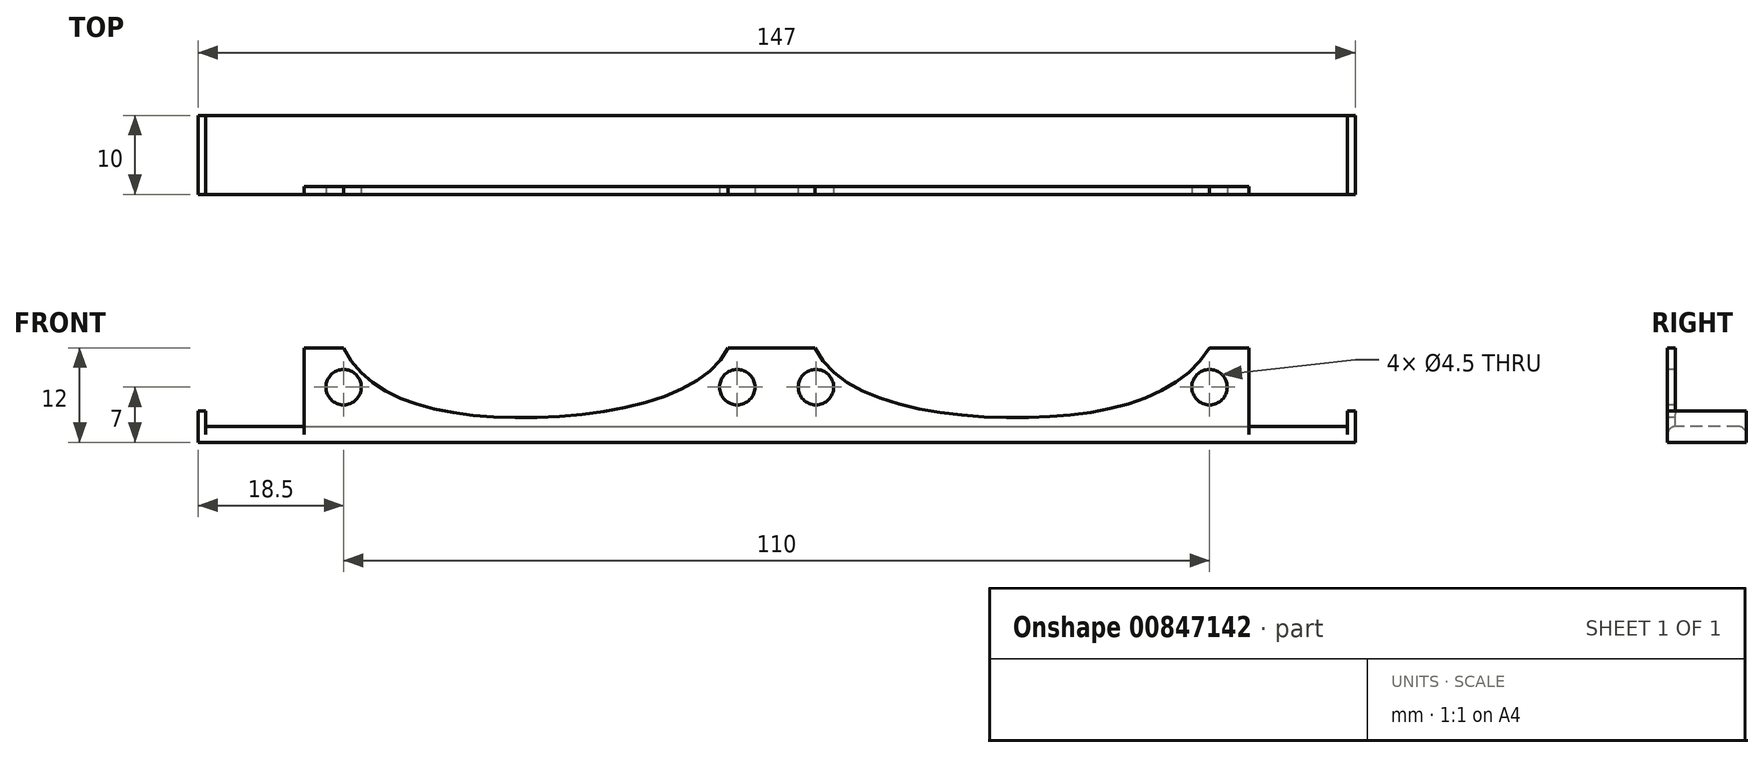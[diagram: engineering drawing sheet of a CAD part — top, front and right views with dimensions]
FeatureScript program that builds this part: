
annotation { "Feature Type Name" : "Feature", "Feature Type Description" : "" }
export const myFeature = defineFeature(function(context is Context, id is Id, definition is map)
    precondition{}
    {
        {
            var Q0;
            Q0=qCreatedBy(makeId("Front.planeOp"),FACE);
            var sketch = newSketch(context, id + "F0", { "sketchPlane" : qUnion([Q0])});
            skLineSegment(sketch, "E0.bottom", {"start": v(-60, 0) * mm, "end": v(60, 0) * mm});
            skLineSegment(sketch, "E0.top", {"start": v(-60, 10) * mm, "end": v(60, 10) * mm});
            skLineSegment(sketch, "E0.left", {"start": v(-60, 0) * mm, "end": v(-60, 10) * mm});
            skLineSegment(sketch, "E0.right", {"start": v(60, 0) * mm, "end": v(60, 10) * mm});
            skPoint(sketch, "E1", {"position": v(0, 0) * mm});
            skPoint(sketch, "E2", {"position": v(-55, 10) * mm});
            skPoint(sketch, "E3", {"position": v(55, 10) * mm});
            skPoint(sketch, "E4", {"position": v(-55, 5) * mm});
            skPoint(sketch, "E5", {"position": v(55, 5) * mm});
            skPoint(sketch, "E6", {"position": v(-5, 5) * mm});
            skPoint(sketch, "E7", {"position": v(5, 5) * mm});
            skFitSpline(sketch, "E8", {"points": [v(-55, 10) * mm, v(-33.54, 1.13) * mm, v(-6.14, 10) * mm], "startDerivative": vector(19.35, -40.47) * mm, "endDerivative": vector(17.4, 37.66) * mm});
            skFitSpline(sketch, "E9", {"points": [v(4.87, 10) * mm, v(31.43, 1.13) * mm, v(55, 10) * mm], "startDerivative": vector(19.32, -40.42) * mm, "endDerivative": vector(24.98, 40.39) * mm});
            skLineSegment(sketch, "E10.top", {"start": v(-60, -2) * mm, "end": v(60, -2) * mm});
            skLineSegment(sketch, "E10.left", {"start": v(-60, 0) * mm, "end": v(-60, -2) * mm});
            skLineSegment(sketch, "E10.right", {"start": v(60, 0) * mm, "end": v(60, -2) * mm});
            skSolve(sketch);
        }
        {
            var Q0;
            {var subQ4=sQuery(id+"F0.wireOp",EDGE,"E0.left");Q0=makeQuery(id+"F0.imprint","IMPRINT",FACE,{"disambiguationData":[TD([[makeQuery(id+"F0.imprint","IMPRINT",EDGE,{"derivedFrom":subQ4}),-1.0]])]});}
            extrude(context, id + "F1", {"entities" : qUnion([Q0]), "oppositeDirection" : true, "depth" : 1 * mm, "offsetDistance" : 25 * mm});
        }
        {
            var Q0;
            Q0=makeQuery(id+"F0.imprint","IMPRINT",FACE,{"disambiguationData":[TD([[makeQuery(id+"F0.imprint","IMPRINT",EDGE,{"derivedFrom":sQuery(id+"F0.wireOp",EDGE,"E0.bottom")}),-1.0]])]});
            extrude(context, id + "F2", {"entities" : qUnion([Q0]), "operationType" : NewBodyOperationType.ADD, "oppositeDirection" : true, "depth" : 10 * mm, "offsetDistance" : 25 * mm});
        }
        {
            var Q0;
            Q0=sQuery(id+"F0.wireOp",VERTEX,"E4");
            var Q1;
            Q1=sQuery(id+"F0.wireOp",VERTEX,"E6");
            var Q2;
            Q2=sQuery(id+"F0.wireOp",VERTEX,"E7");
            var Q3;
            Q3=sQuery(id+"F0.wireOp",VERTEX,"E5");
            var Q4;
            Q4=makeQuery(id+"F1.opExtrude","SWEPT_BODY",BODY,{"disambiguationData":[OSD([sQuery(id+"F0.wireOp",EDGE,"E0.top"),sQuery(id+"F0.wireOp",EDGE,"E0.left"),sQuery(id+"F0.wireOp",EDGE,"E0.right"),sQuery(id+"F0.wireOp",EDGE,"E8"),sQuery(id+"F0.wireOp",EDGE,"E9"),sQuery(id+"F0.wireOp",EDGE,"E0.bottom")])]});
            hole(context, id + "F3", {"style" : HoleStyle.SIMPLE, "endStyle" : HoleEndStyle.BLIND, "holeDiameter" : 4.5 * mm, "majorDiameter" : 5 * mm, "holeDepth" : 2 * mm, "isTappedThrough" : true, "tappedDepth" : 12 * mm, "tapClearance" : 3, "locations" : qUnion([Q0, Q1, Q2, Q3]), "scope" : qUnion([Q4])});
        }
        {
            var Q0;
            Q0=makeQuery(id+"F2.boolean.opBoolean","MERGE",FACE,{"derivedFrom":[makeQuery(id+"F1.opExtrude","SWEPT_FACE",FACE,{"disambiguationData":[OSD([sQuery(id+"F0.wireOp",EDGE,"E0.left")])]}),makeQuery(id+"F2.opExtrude","SWEPT_FACE",FACE,{"disambiguationData":[OSD([sQuery(id+"F0.wireOp",EDGE,"E10.left")])]})]});
            var sketch = newSketch(context, id + "F4", { "sketchPlane" : qUnion([Q0])});
            skLineSegment(sketch, "E11.bottom", {"start": v(-10, 0) * mm, "end": v(0, 0) * mm});
            skLineSegment(sketch, "E11.top", {"start": v(-10, -2) * mm, "end": v(0, -2) * mm});
            skLineSegment(sketch, "E11.left", {"start": v(-10, 0) * mm, "end": v(-10, -2) * mm});
            skLineSegment(sketch, "E11.right", {"start": v(0, 0) * mm, "end": v(0, -2) * mm});
            skSolve(sketch);
        }
        {
            var Q0;
            Q0=makeQuery(id+"F4.imprint","IMPRINT",FACE,{"disambiguationData":[TD([[makeQuery(id+"F4.imprint","IMPRINT",EDGE,{"derivedFrom":sQuery(id+"F4.wireOp",EDGE,"E11.top")}),1.0]])]});
            extrude(context, id + "F5", {"entities" : qUnion([Q0]), "operationType" : NewBodyOperationType.ADD, "depth" : 13.5 * mm, "offsetDistance" : 25 * mm});
        }
        {
            var Q0;
            Q0=makeQuery(id+"F2.boolean.opBoolean","MERGE",FACE,{"derivedFrom":[makeQuery(id+"F1.opExtrude","SWEPT_FACE",FACE,{"disambiguationData":[OSD([sQuery(id+"F0.wireOp",EDGE,"E0.right")])]}),makeQuery(id+"F2.opExtrude","SWEPT_FACE",FACE,{"disambiguationData":[OSD([sQuery(id+"F0.wireOp",EDGE,"E10.right")])]})]});
            var sketch = newSketch(context, id + "F6", { "sketchPlane" : qUnion([Q0])});
            skLineSegment(sketch, "E12.bottom", {"start": v(0, -2) * mm, "end": v(10, -2) * mm});
            skLineSegment(sketch, "E12.top", {"start": v(0, 0) * mm, "end": v(10, 0) * mm});
            skLineSegment(sketch, "E12.left", {"start": v(0, -2) * mm, "end": v(0, 0) * mm});
            skLineSegment(sketch, "E12.right", {"start": v(10, -2) * mm, "end": v(10, 0) * mm});
            skSolve(sketch);
        }
        {
            var Q0;
            Q0=makeQuery(id+"F6.imprint","IMPRINT",FACE,{"disambiguationData":[TD([[makeQuery(id+"F6.imprint","IMPRINT",EDGE,{"derivedFrom":sQuery(id+"F6.wireOp",EDGE,"E12.bottom")}),-1.0]])]});
            extrude(context, id + "F7", {"entities" : qUnion([Q0]), "operationType" : NewBodyOperationType.ADD, "depth" : 13.5 * mm, "offsetDistance" : 25 * mm});
        }
        {
            var Q0;
            Q0=makeQuery(id+"F7.boolean.opBoolean","MERGE",FACE,{"derivedFrom":[makeQuery(id+"F5.boolean.opBoolean","MERGE",FACE,{"derivedFrom":[makeQuery(id+"F2.opExtrude","SWEPT_FACE",FACE,{"disambiguationData":[OSD([sQuery(id+"F0.wireOp",EDGE,"E0.bottom")])]}),makeQuery(id+"F5.opExtrude","SWEPT_FACE",FACE,{"disambiguationData":[OSD([sQuery(id+"F4.wireOp",EDGE,"E11.bottom")])]})]}),makeQuery(id+"F7.opExtrude","SWEPT_FACE",FACE,{"disambiguationData":[OSD([sQuery(id+"F6.wireOp",EDGE,"E12.top")])]})]});
            var sketch = newSketch(context, id + "F8", { "sketchPlane" : qUnion([Q0])});
            skLineSegment(sketch, "E13.bottom", {"start": v(-73.5, 10) * mm, "end": v(-72.5, 10) * mm});
            skLineSegment(sketch, "E13.top", {"start": v(-73.5, 0) * mm, "end": v(-72.5, 0) * mm});
            skLineSegment(sketch, "E13.left", {"start": v(-73.5, 10) * mm, "end": v(-73.5, 0) * mm});
            skLineSegment(sketch, "E13.right", {"start": v(-72.5, 10) * mm, "end": v(-72.5, 0) * mm});
            skLineSegment(sketch, "E14.bottom", {"start": v(73.5, 10) * mm, "end": v(72.5, 10) * mm});
            skLineSegment(sketch, "E14.top", {"start": v(73.5, 0) * mm, "end": v(72.5, 0) * mm});
            skLineSegment(sketch, "E14.left", {"start": v(73.5, 10) * mm, "end": v(73.5, 0) * mm});
            skLineSegment(sketch, "E14.right", {"start": v(72.5, 10) * mm, "end": v(72.5, 0) * mm});
            skSolve(sketch);
        }
        {
            var Q0;
            Q0=makeQuery(id+"F8.imprint","IMPRINT",FACE,{"disambiguationData":[TD([[makeQuery(id+"F8.imprint","IMPRINT",EDGE,{"derivedFrom":sQuery(id+"F8.wireOp",EDGE,"E13.bottom")}),-1.0]])]});
            var Q1;
            Q1=makeQuery(id+"F8.imprint","IMPRINT",FACE,{"disambiguationData":[TD([[makeQuery(id+"F8.imprint","IMPRINT",EDGE,{"derivedFrom":sQuery(id+"F8.wireOp",EDGE,"E14.bottom")}),-1.0]])]});
            extrude(context, id + "F9", {"entities" : qUnion([Q0, Q1]), "operationType" : NewBodyOperationType.ADD, "depth" : 2 * mm, "offsetDistance" : 25 * mm});
        }
        {
            var Q0;
            Q0=makeQuery(id+"F7.boolean.opBoolean","MERGE",EDGE,{"derivedFrom":[makeQuery(id+"F5.boolean.opBoolean","MERGE",EDGE,{"derivedFrom":[makeQuery(id+"F2.opExtrude","CAP_EDGE",EDGE,{"disambiguationData":[OSD([sQuery(id+"F0.wireOp",EDGE,"E0.bottom")])],"isStart":false}),makeQuery(id+"F5.opExtrude","SWEPT_EDGE",EDGE,{"disambiguationData":[OSD([sQuery(id+"F4.wireOp",EDGE,"E11.bottom"),sQuery(id+"F4.wireOp",EDGE,"E11.left")])]})]}),makeQuery(id+"F7.opExtrude","SWEPT_EDGE",EDGE,{"disambiguationData":[OSD([sQuery(id+"F6.wireOp",EDGE,"E12.top"),sQuery(id+"F6.wireOp",EDGE,"E12.right")])]})]});
            var Q1;
            Q1=makeQuery(id+"F5.opExtrude","SWEPT_EDGE",EDGE,{"disambiguationData":[OSD([sQuery(id+"F0.wireOp",EDGE,"E0.left"),sQuery(id+"F0.wireOp",EDGE,"E10.left"),sQuery(id+"F4.wireOp",EDGE,"E11.bottom"),sQuery(id+"F4.wireOp",EDGE,"E11.right")])]});
            var Q2;
            Q2=makeQuery(id+"F7.opExtrude","SWEPT_EDGE",EDGE,{"disambiguationData":[OSD([sQuery(id+"F0.wireOp",EDGE,"E0.right"),sQuery(id+"F0.wireOp",EDGE,"E10.right"),sQuery(id+"F6.wireOp",EDGE,"E12.top"),sQuery(id+"F6.wireOp",EDGE,"E12.left")])]});
            fillet(context, id + "F10", {"entities" : qUnion([Q0, Q1, Q2]), "radius" : 1 * mm, "tangentPropagation" : true, "allowEdgeOverflow" : false});
        }
    });
